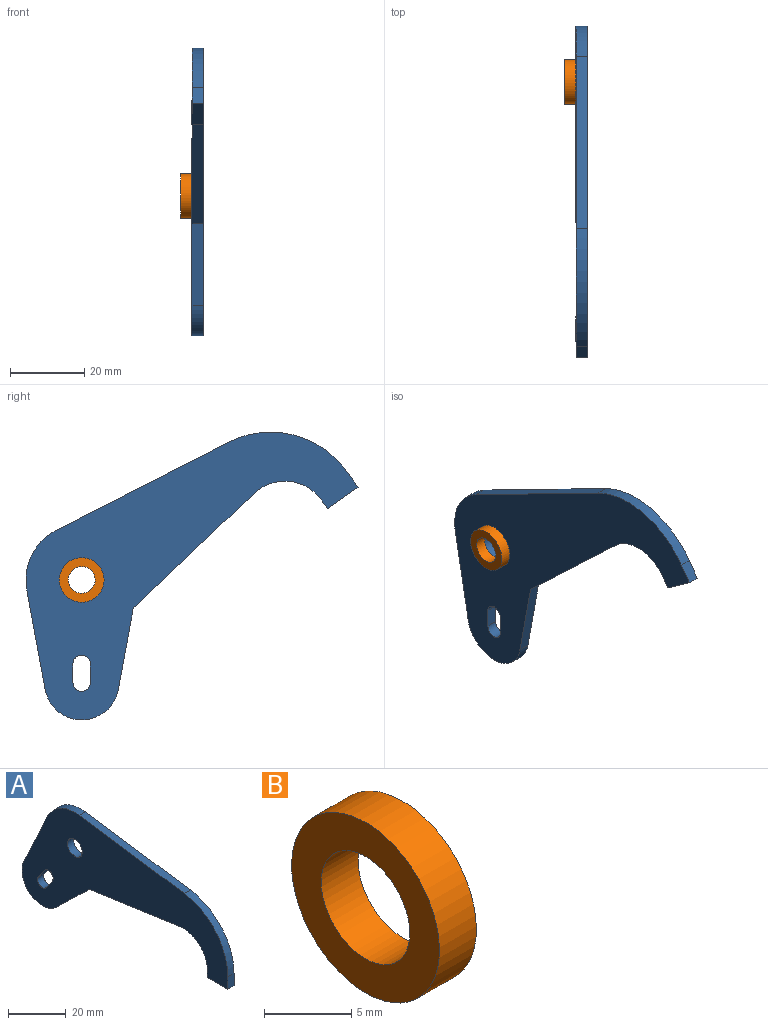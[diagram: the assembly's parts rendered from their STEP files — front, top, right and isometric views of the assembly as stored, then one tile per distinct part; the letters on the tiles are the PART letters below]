
ASSEMBLY  parts=2 mates=1
PART A: 18 faces, bbox 3x101x47.6 mm
  f0: plane 100.95x47.55mm, normal (1,0,0), area 2358.5mm2, adj f1,f2,f3,f4,f5,f6,f7,f8
  f1: cylinder r=2.35mm len=4.27mm, axis (-1,0,0), area 22.1mm2, adj f0,f2,f16,f17
  f2: plane 4.14x3mm, normal (0,0.82,0.58), area 15.2mm2, adj f0,f1,f3,f17
  f3: cylinder r=2.35mm len=4.27mm, axis (-1,0,0), area 22.1mm2, adj f0,f2,f16,f17
  f4: plane 44.31x6.4mm, normal (0,-0.14,-0.99), area 134.3mm2, adj f0,f5,f15,f17
  f5: plane 15.95x15.56mm, normal (0,-0.7,-0.72), area 66.8mm2, adj f0,f4,f6,f17
  f6: cylinder r=10mm len=16.98mm, axis (-1,0,0), area 83.3mm2, adj f0,f5,f7,f17
  f7: plane 24.65x11.41mm, normal (0,0.91,0.42), area 81.5mm2, adj f0,f6,f8,f17
  f8: cylinder r=15mm len=15.75mm, axis (-1,0,0), area 57.6mm2, adj f0,f7,f9,f17
  f9: plane 51.43x7.42mm, normal (0,-0.14,0.99), area 155.9mm2, adj f0,f8,f10,f17
  f10: cylinder r=25mm len=24.74mm, axis (-1,0,0), area 107.1mm2, adj f0,f9,f11,f17
  f11: plane 5.23x3mm, normal (0,-1,0), area 15.7mm2, adj f0,f10,f12,f17
  f12: plane 10x3mm, normal (0,0,-1), area 30mm2, adj f0,f11,f13,f17
  f13: plane 3x2.92mm, normal (0,1,0), area 8.8mm2, adj f0,f12,f15,f17
  f14: cylinder r=3.6mm len=7.2mm, axis (-1,0,0), area 67.9mm2, adj f0,f17
  f15: cylinder r=12mm len=13.71mm, axis (-1,0,0), area 61.7mm2, adj f0,f4,f13,f17
  f16: plane 4.14x3mm, normal (0,-0.82,-0.58), area 15.2mm2, adj f0,f1,f3,f17
  f17: plane 100.95x47.55mm, normal (-1,0,0), area 2358.5mm2, adj f1,f2,f3,f4,f5,f6,f7,f8
PART B: 4 faces, bbox 3x12x12 mm
  f0: plane 12x12mm, normal (1,0,0), area 72.4mm2, adj f1,f2
  f1: cylinder r=3.6mm len=7.2mm, axis (-1,0,0), area 67.9mm2, adj f0,f3
  f2: cylinder r=6mm len=12mm, axis (-1,0,0), area 113.1mm2, adj f0,f3
  f3: plane 12x12mm, normal (-1,0,0), area 72.4mm2, adj f1,f2
PLACE A rot(axis=(-1,0,0),35.3deg) t=(-60.35,16.91,20.25)mm
PLACE B rot(axis=(-1,0,0),35.3deg) t=(-66.35,16.91,20.25)mm
MATE fastened A.f8 <-> B.f1  axis (-1,0,0) through (-48.35,10.42,52.46)mm
